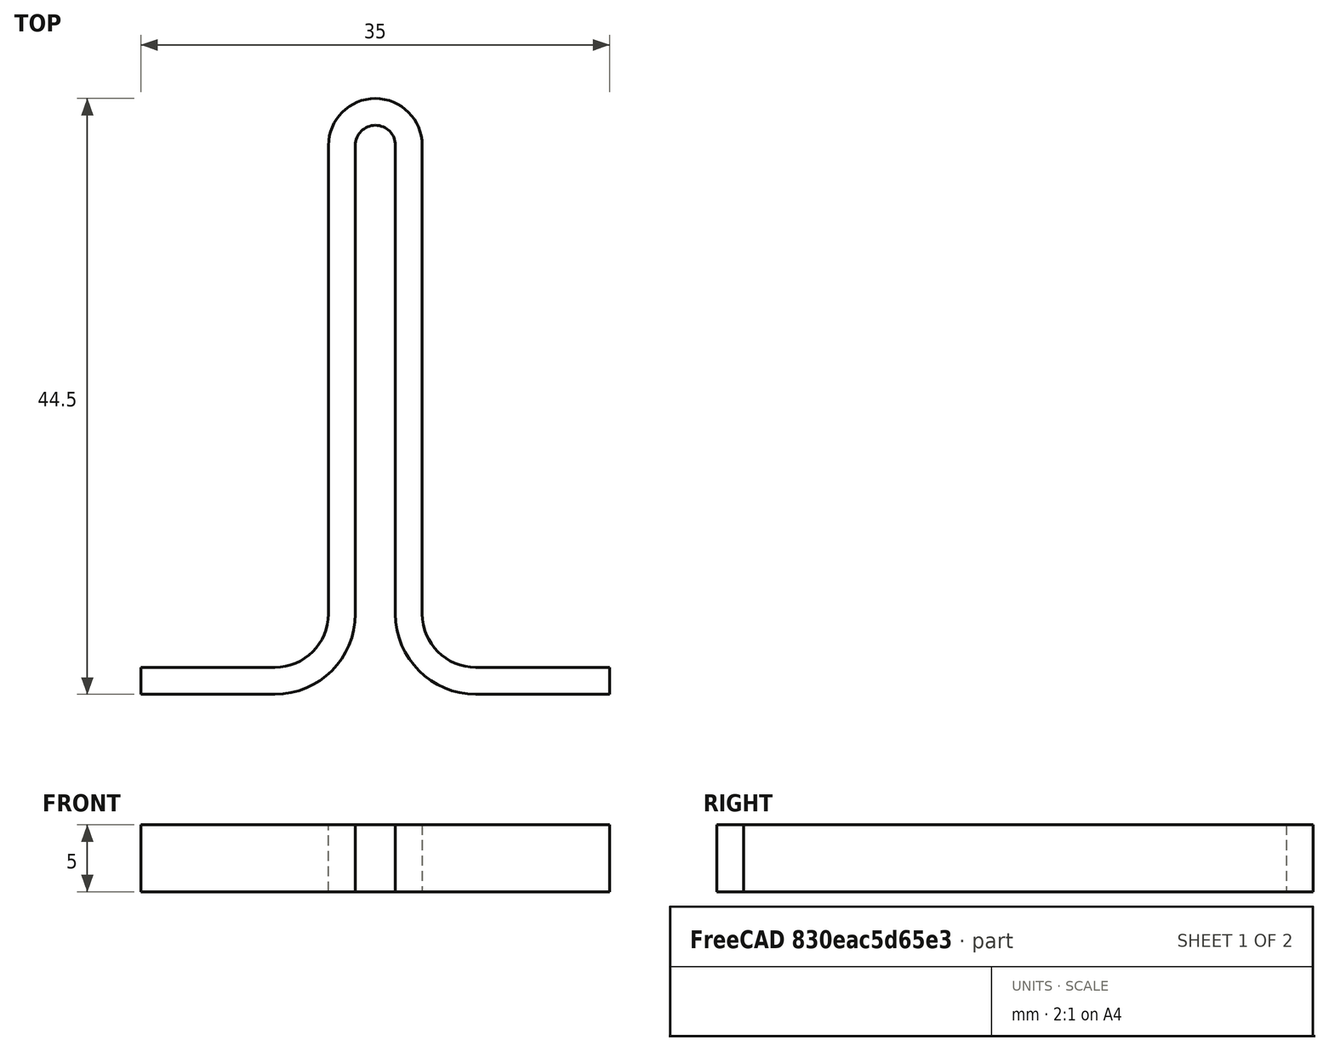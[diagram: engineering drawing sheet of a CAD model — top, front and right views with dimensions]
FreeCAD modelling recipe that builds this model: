
FCSTD DOCUMENT  (FreeCAD 2021.1015R24301 +3962 (Git))
Label: plastic_spring_long_single_loop
License: All rights reserved
objects: Sketcher::SketchObject×2, Mesh::Feature×2, Spreadsheet::Sheet×1, PartDesign::AdditivePipe×1, PartDesign::Body×1
note: 6 computed .brp shape members not serialized (recipe doc carries the construction recipe); baked Part::Feature solids carry a one-line shape summary decoded from their .brp

FEATURE [Spreadsheet::Sheet] Spreadsheet
  PythonMode = false
  cells = A1='height; B1(h)=5; A2='thickness; B2(thk)=2; A3='dia; B3(dia)=5; A4=start finish rad; B4(r_start)=5; A5=center length; B5(l_center)=40; A6=center spacing; B6(cs)=7; C6=should be dia/2 really; A7=end length; B7(l_end)=10
FEATURE [Sketcher::SketchObject] Sketch  label="profile"
  FullyConstrained = true
  MapMode = 5
  Placement = pos=(0,0,0) rot=(0.57735,0.57735,0.57735;2.0944rad)
  Support = -> [YZ_Plane]
  expr: Constraints[10] = Spreadsheet.thk / 2
  expr: Constraints[11] = Spreadsheet.thk
  expr: Constraints[9] = Spreadsheet.h
  sketch-geometry (4):
    g0: LineSegment StartX=-1 StartY=0 StartZ=0 EndX=1 EndY=0 EndZ=0
    g1: LineSegment StartX=1 StartY=0 StartZ=0 EndX=1 EndY=5 EndZ=0
    g2: LineSegment StartX=1 StartY=5 StartZ=0 EndX=-1 EndY=5 EndZ=0
    g3: LineSegment StartX=-1 StartY=5 StartZ=0 EndX=-1 EndY=0 EndZ=0
  constraints (12):
    c: Coincident(g0,g1)
    c: Coincident(g1,g2)
    c: Coincident(g2,g3)
    c: Coincident(g3,g0)
    c: Horizontal(g0)
    c: Horizontal(g2)
    c: Vertical(g1)
    c: Vertical(g3)
    c: PointOnObject(g0,g-1)
    c: DistanceY(g3,g3) = 5
    c: DistanceX(g0,g-1) = 1
    c: DistanceX(g0,g0) = 2
FEATURE [Sketcher::SketchObject] Sketch001  label="path"
  FullyConstrained = true
  MapMode = 5
  Support = -> [XY_Plane]
  expr: Constraints[12] = Spreadsheet.l_end
  expr: Constraints[13] = Spreadsheet.dia
  expr: Constraints[14] = Spreadsheet.l_end
  expr: Constraints[17] = Spreadsheet.r_start
  expr: Constraints[18] = Spreadsheet.r_start
  expr: Constraints[19] = Spreadsheet.l_center
  expr: Constraints[22] = Spreadsheet.dia
  sketch-geometry (7):
    g0: LineSegment StartX=0 StartY=0 StartZ=0 EndX=10 EndY=6.8754e-12 EndZ=0
    g1: LineSegment StartX=15 StartY=5 StartZ=0 EndX=15 EndY=40 EndZ=0
    g2: ArcOfCircle CenterX=10 CenterY=5 CenterZ=0 NormalX=0 NormalY=0 NormalZ=1 AngleXU=0 Radius=5 StartAngle=4.71239 EndAngle=6.28319
    g3: ArcOfCircle CenterX=17.5 CenterY=40 CenterZ=0 NormalX=0 NormalY=0 NormalZ=1 AngleXU=0 Radius=2.5 StartAngle=6.28318 EndAngle=9.42478
    g4: LineSegment StartX=20 StartY=40 StartZ=0 EndX=20 EndY=5 EndZ=0
    g5: LineSegment StartX=25 StartY=0 StartZ=0 EndX=35 EndY=0 EndZ=0
    g6: ArcOfCircle CenterX=25 CenterY=5 CenterZ=0 NormalX=0 NormalY=0 NormalZ=1 AngleXU=0 Radius=5 StartAngle=3.14159 EndAngle=4.71239
  constraints (24):
    c: Coincident(g0,g-1)
    c: PointOnObject(g0,g-1)
    c: Coincident(g2,g0)
    c: Coincident(g2,g1)
    c: Coincident(g3,g1)
    c: Coincident(g4,g3)
    c: PointOnObject(g5,g-1)
    c: PointOnObject(g5,g-1)
    c: Tangent(g0,g2)
    c: Tangent(g2,g1)
    c: Tangent(g1,g3)
    c: Tangent(g3,g4)
    c: DistanceX(g5,g5) = 10
    c: Diameter(g3) = 5
    c: DistanceX(g0,g0) = 10
    c: Coincident(g6,g4)
    c: Coincident(g6,g5)
    c: Radius(g2) = 5
    c: Radius(g6) = 5
    c: DistanceY(g0,g3) = 40
    c: Tangent(g6,g5)
    c: Tangent(g6,g4)
    c: DistanceX(g1,g4) = 5
    c: Vertical(g1)
FEATURE [PartDesign::AdditivePipe] AdditivePipe
  AuxilleryCurvelinear = true
  AuxillerySpineTangent = false
  Binormal = (0,0,0)
  ClaimChildren = false
  Fit = 0
  FitJoin = 0
  InnerFit = 0
  InnerFitJoin = 0
  Mode = 0
  NewSolid = false
  Placement = pos=(0,0,0) rot=(0.57735,0.57735,0.57735;2.0944rad)
  Profile = -> Sketch
  Spine = -> Sketch001
  SpineTangent = false
  Suppress = false
  Transformation = 0
  Transition = 1
  _ProfileBasedVersion = 1
FEATURE [PartDesign::Body] Body
  AutoGroupSolids = false
  ExportMode = 0
  Group = -> [Sketch,Sketch001,AdditivePipe]
  Origin = -> Origin
  Tip = -> AdditivePipe
  _ExportChildren = -> [AdditivePipe]
  _GroupVersion = 1
FEATURE [Mesh::Feature] Mesh  label="single_loop_40x5x1thk"
FEATURE [Mesh::Feature] Mesh001  label="single_loop_40x5x2thk"
